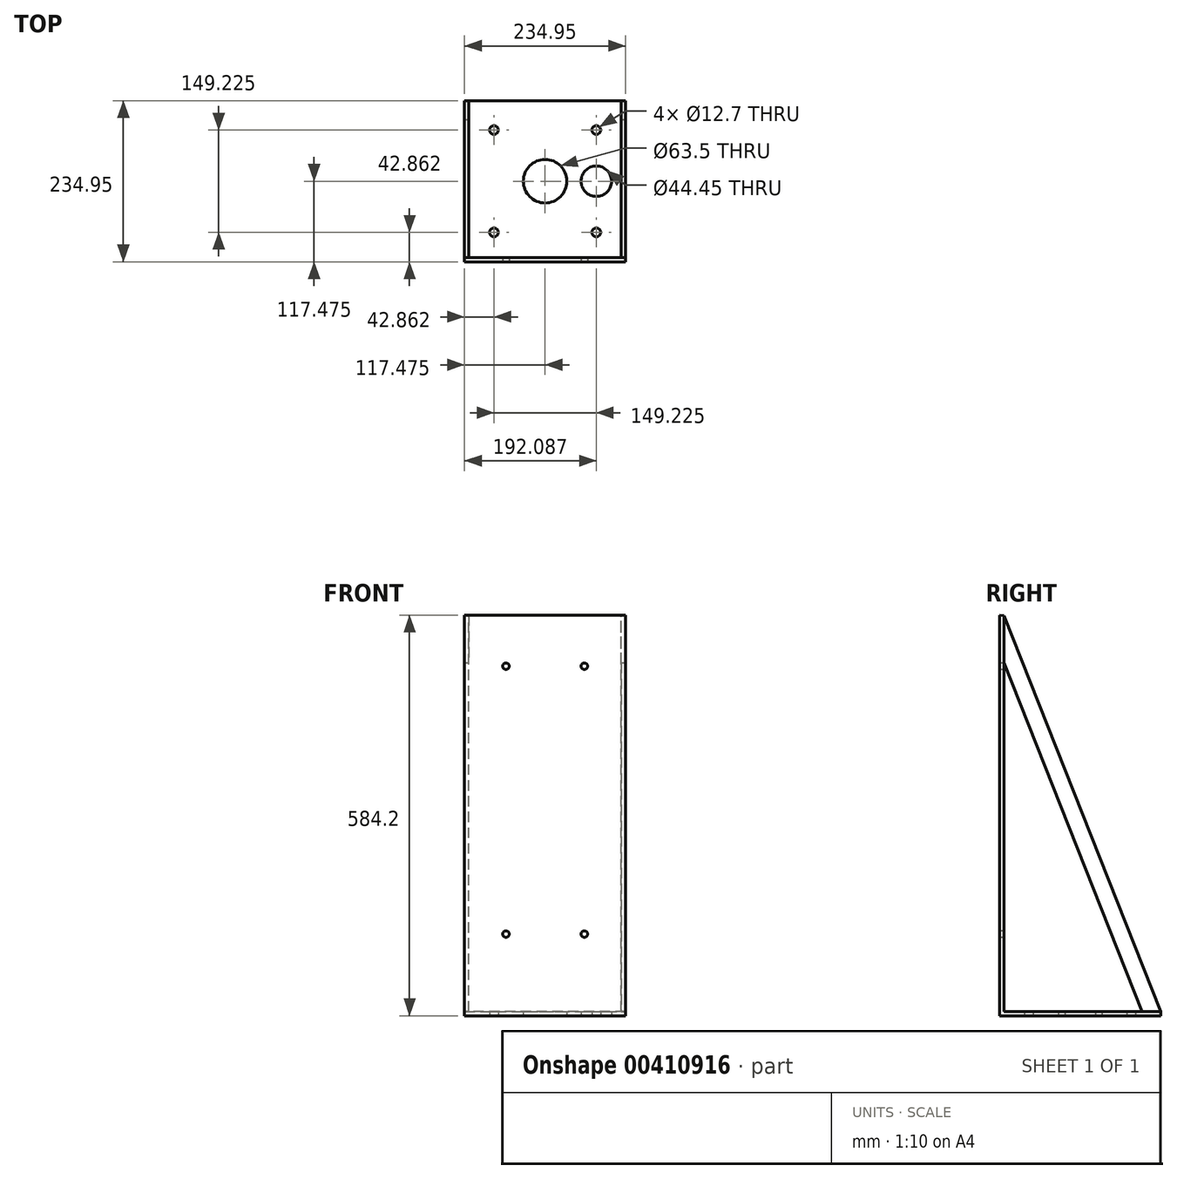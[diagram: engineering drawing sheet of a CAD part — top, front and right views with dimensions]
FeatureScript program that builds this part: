
annotation { "Feature Type Name" : "Feature", "Feature Type Description" : "" }
export const myFeature = defineFeature(function(context is Context, id is Id, definition is map)
    precondition{}
    {
        {
            var Q0;
            Q0=qCreatedBy(makeId("Top.planeOp"),FACE);
            var sketch = newSketch(context, id + "F0", { "sketchPlane" : qUnion([Q0])});
            skLineSegment(sketch, "E0", {"start": v(0, 0) * mm, "end": v(-234.95, 0) * mm});
            skLineSegment(sketch, "E1", {"start": v(-234.95, 0) * mm, "end": v(-234.95, 234.95) * mm});
            skLineSegment(sketch, "E2", {"start": v(-234.95, 234.95) * mm, "end": v(0, 234.95) * mm});
            skLineSegment(sketch, "E3", {"start": v(0, 234.95) * mm, "end": v(0, 0) * mm});
            skSolve(sketch);
        }
        {
            var Q0;
            Q0=qSketchRegion(id+"F0",true);
            extrude(context, id + "F1", {"entities" : qUnion([Q0]), "depth" : 584.2 * mm});
        }
        {
            var Q0;
            Q0=makeQuery(id+"F1.opExtrude","SWEPT_FACE",FACE,{"disambiguationData":[OSD([sQuery(id+"F0.wireOp",EDGE,"E3")])]});
            var sketch = newSketch(context, id + "F2", { "sketchPlane" : qUnion([Q0])});
            skLineSegment(sketch, "E4", {"start": v(234.95, 558.8) * mm, "end": v(0, 584.2) * mm});
            skLineSegment(sketch, "E5", {"start": v(234.95, 558.8) * mm, "end": v(234.95, 584.2) * mm});
            skLineSegment(sketch, "E6", {"start": v(234.95, 584.2) * mm, "end": v(0, 584.2) * mm});
            skSolve(sketch);
        }
        {
            var Q0;
            Q0=makeQuery(id+"F2.imprint","IMPRINT",FACE,{"disambiguationData":[TD([[makeQuery(id+"F2.imprint","IMPRINT",EDGE,{"derivedFrom":sQuery(id+"F2.wireOp",EDGE,"E4")}),-1.0]])]});
            extrude(context, id + "F3", {"entities" : qUnion([Q0]), "operationType" : NewBodyOperationType.REMOVE, "endBound" : BoundingType.THROUGH_ALL, "oppositeDirection" : true, "depth" : 25.4 * mm});
        }
        {
            var Q0;
            {var subQ0=sQuery(id+"F0.wireOp",EDGE,"E0");Q0=makeQuery(id+"FEAy7TYS6UcWf4X_1.boolean.opBoolean","MERGE",FACE,{"derivedFrom":[makeQuery(id+"F1.opExtrude","SWEPT_FACE",FACE,{"disambiguationData":[OSD([subQ0])]}),makeQuery(id+"FEAy7TYS6UcWf4X_1.opExtrude","SWEPT_FACE",FACE,{"disambiguationData":[OSD([subQ0])]})]});}
            var sketch = newSketch(context, id + "F4", { "sketchPlane" : qUnion([Q0])});
            skLineSegment(sketch, "E7", {"start": v(-117.48, 0) * mm, "end": v(-117.48, 509.59) * mm});
            skPoint(sketch, "E8.endSnap0", {"position": v(-117.47, 584.2) * mm});
            skLineSegment(sketch, "E9", {"start": v(-117.48, 509.59) * mm, "end": v(-60.33, 509.59) * mm});
            skLineSegment(sketch, "E10", {"start": v(-117.48, 509.59) * mm, "end": v(-174.63, 509.59) * mm});
            skCircle(sketch, "E11", {"center": v(-60.33, 509.59) * mm, "radius": 4.76 * mm});
            skCircle(sketch, "E12", {"center": v(-174.63, 509.59) * mm, "radius": 4.76 * mm});
            skLineSegment(sketch, "E13", {"start": v(-174.63, 509.59) * mm, "end": v(-174.62, 119.06) * mm});
            skLineSegment(sketch, "E14", {"start": v(-60.33, 509.59) * mm, "end": v(-60.33, 119.06) * mm});
            skCircle(sketch, "E15", {"center": v(-174.62, 119.06) * mm, "radius": 4.76 * mm});
            skCircle(sketch, "E16", {"center": v(-60.33, 119.06) * mm, "radius": 4.76 * mm});
            skSolve(sketch);
        }
        {
            var Q0;
            Q0=qSketchRegion(id+"F4",true);
            extrude(context, id + "F5", {"entities" : qUnion([Q0]), "operationType" : NewBodyOperationType.REMOVE, "oppositeDirection" : true, "depth" : 25.4 * mm});
        }
        {
            var Q0;
            Q0=qSketchRegion(id+"F4",true);
            extrude(context, id + "F6", {"entities" : qUnion([Q0]), "operationType" : NewBodyOperationType.REMOVE, "oppositeDirection" : true, "depth" : 25.4 * mm});
        }
        {
            var Q0;
            Q0=makeQuery(id+"F1.opExtrude","SWEPT_FACE",FACE,{"disambiguationData":[OSD([sQuery(id+"F0.wireOp",EDGE,"E3")])]});
            var sketch = newSketch(context, id + "F7", { "sketchPlane" : qUnion([Q0])});
            skLineSegment(sketch, "E17", {"start": v(0, 0) * mm, "end": v(6.35, 0) * mm});
            skLineSegment(sketch, "E18", {"start": v(6.35, 0) * mm, "end": v(6.35, 6.35) * mm});
            skLineSegment(sketch, "E19.bottom", {"start": v(6.35, 6.35) * mm, "end": v(445.92, 6.35) * mm});
            skLineSegment(sketch, "E19.top", {"start": v(6.35, 612) * mm, "end": v(445.92, 612) * mm});
            skLineSegment(sketch, "E19.left", {"start": v(6.35, 6.35) * mm, "end": v(6.35, 612) * mm});
            skLineSegment(sketch, "E19.right", {"start": v(445.92, 6.35) * mm, "end": v(445.92, 612) * mm});
            skSolve(sketch);
        }
        {
            var Q0;
            Q0 = qSketchRegion(id + "F7", true);
            extrude(context, id + "F8", {"entities" : qUnion([Q0]), "operationType" : NewBodyOperationType.REMOVE, "endBound" : BoundingType.THROUGH_ALL, "oppositeDirection" : true, "depth" : 25.4 * mm});
        }
        {
            var Q0;
            Q0=makeQuery(id+"F1.opExtrude","SWEPT_FACE",FACE,{"disambiguationData":[OSD([sQuery(id+"F0.wireOp",EDGE,"E3")])]});
            var sketch = newSketch(context, id + "F9", { "sketchPlane" : qUnion([Q0])});
            skLineSegment(sketch, "E20", {"start": v(6.35, 583.51) * mm, "end": v(6.35, 6.35) * mm});
            skLineSegment(sketch, "E21", {"start": v(6.35, 6.35) * mm, "end": v(234.95, 6.35) * mm});
            skLineSegment(sketch, "E22", {"start": v(234.95, 6.35) * mm, "end": v(6.35, 583.51) * mm});
            skSolve(sketch);
        }
        {
            var Q0;
            Q0 = qSketchRegion(id + "F9", true);
            extrude(context, id + "F10", {"entities" : qUnion([Q0]), "oppositeDirection" : true, "depth" : 6.35 * mm});
        }
        {
            var Q0;
            Q0=makeQuery(id+"F1.opExtrude","SWEPT_FACE",FACE,{"disambiguationData":[OSD([sQuery(id+"F0.wireOp",EDGE,"E1")])]});
            var sketch = newSketch(context, id + "F11", { "sketchPlane" : qUnion([Q0])});
            skLineSegment(sketch, "E23", {"start": v(-6.35, 583.51) * mm, "end": v(-6.35, 6.35) * mm});
            skLineSegment(sketch, "E24", {"start": v(-6.35, 6.35) * mm, "end": v(-234.95, 6.35) * mm});
            skLineSegment(sketch, "E25", {"start": v(-234.95, 6.35) * mm, "end": v(-6.35, 583.51) * mm});
            skSolve(sketch);
        }
        {
            var Q0;
            Q0 = qSketchRegion(id + "F11", true);
            extrude(context, id + "F12", {"entities" : qUnion([Q0]), "operationType" : NewBodyOperationType.ADD, "oppositeDirection" : true, "depth" : 6.35 * mm});
        }
        {
            var Q0;
            Q0=makeQuery(id+"F1.opExtrude","CAP_FACE",FACE,{"disambiguationData":[OSD([sQuery(id+"F0.wireOp",EDGE,"E0"),sQuery(id+"F0.wireOp",EDGE,"E1"),sQuery(id+"F0.wireOp",EDGE,"E2"),sQuery(id+"F0.wireOp",EDGE,"E3")])],"isStart":true});
            var sketch = newSketch(context, id + "F13", { "sketchPlane" : qUnion([Q0])});
            skCircle(sketch, "E26", {"center": v(-192.09, -42.86) * mm, "radius": 6.35 * mm});
            skCircle(sketch, "E27", {"center": v(-42.86, -42.86) * mm, "radius": 6.35 * mm});
            skCircle(sketch, "E28", {"center": v(-42.86, -192.09) * mm, "radius": 6.35 * mm});
            skCircle(sketch, "E29", {"center": v(-192.09, -192.09) * mm, "radius": 6.35 * mm});
            skCircle(sketch, "E30", {"center": v(-42.86, -117.48) * mm, "radius": 22.23 * mm});
            skCircle(sketch, "E31", {"center": v(-117.47, -117.48) * mm, "radius": 31.75 * mm});
            skSolve(sketch);
        }
        {
            var Q0;
            Q0 = qSketchRegion(id + "F13", true);
            extrude(context, id + "F14", {"entities" : qUnion([Q0]), "operationType" : NewBodyOperationType.REMOVE, "endBound" : BoundingType.THROUGH_ALL, "oppositeDirection" : true, "depth" : 25.4 * mm});
        }
        {
            var Q0;
            Q0 = qSketchRegion(id + "F13", true);
            extrude(context, id + "F15", {"entities" : qUnion([Q0]), "operationType" : NewBodyOperationType.REMOVE, "oppositeDirection" : true, "depth" : 25.4 * mm});
        }
        {
            var Q0;
            Q0=makeQuery(id+"F10.opExtrude","CAP_FACE",FACE,{"disambiguationData":[OSD([sQuery(id+"F9.wireOp",EDGE,"E20"),sQuery(id+"F9.wireOp",EDGE,"E21"),sQuery(id+"F9.wireOp",EDGE,"E22")])],"isStart":true});
            var sketch = newSketch(context, id + "F16", { "sketchPlane" : qUnion([Q0])});
            skLineSegment(sketch, "E32", {"start": v(97.03, 285.58) * mm, "end": v(6.35, 514.54) * mm});
            skLineSegment(sketch, "E33", {"start": v(97.03, 285.58) * mm, "end": v(207.63, 6.35) * mm});
            skSolve(sketch);
        }
        {
            var Q0;
            {var subQ0=sQuery(id+"F16.wireOp",EDGE,"E32");Q0=makeQuery(id+"F16.imprint","IMPRINT",FACE,{"disambiguationData":[TD([[makeQuery(id+"F16.imprint","IMPRINT",EDGE,{"derivedFrom":subQ0}),1.0]])]});}
            extrude(context, id + "F17", {"entities" : qUnion([Q0]), "operationType" : NewBodyOperationType.REMOVE, "endBound" : BoundingType.THROUGH_ALL, "oppositeDirection" : true, "depth" : 254 * mm});
        }
        {
            var Q0;
            Q0=makeQuery(id+"F12.boolean.opBoolean","MERGE",FACE,{"derivedFrom":[makeQuery(id+"F1.opExtrude","SWEPT_FACE",FACE,{"disambiguationData":[OSD([sQuery(id+"F0.wireOp",EDGE,"E1")])]}),makeQuery(id+"F12.opExtrude","CAP_FACE",FACE,{"disambiguationData":[OSD([sQuery(id+"F11.wireOp",EDGE,"E23"),sQuery(id+"F11.wireOp",EDGE,"E24"),sQuery(id+"F11.wireOp",EDGE,"E25")])],"isStart":true})]});
            var sketch = newSketch(context, id + "F18", { "sketchPlane" : qUnion([Q0])});
            skLineSegment(sketch, "E34", {"start": v(-97.03, 285.58) * mm, "end": v(-6.35, 514.54) * mm});
            skLineSegment(sketch, "E35", {"start": v(-6.35, 514.54) * mm, "end": v(-6.35, 6.35) * mm});
            skLineSegment(sketch, "E36", {"start": v(-97.03, 285.58) * mm, "end": v(-207.63, 6.35) * mm});
            skLineSegment(sketch, "E37", {"start": v(-207.63, 6.35) * mm, "end": v(-6.35, 6.35) * mm});
            skSolve(sketch);
        }
        {
            var Q0;
            Q0=makeQuery(id+"F18.imprint","IMPRINT",FACE,{"disambiguationData":[TD([[makeQuery(id+"F18.imprint","IMPRINT",EDGE,{"derivedFrom":sQuery(id+"F18.wireOp",EDGE,"E34")}),-1.0]])]});
            extrude(context, id + "F19", {"entities" : qUnion([Q0]), "operationType" : NewBodyOperationType.REMOVE, "endBound" : BoundingType.THROUGH_ALL, "oppositeDirection" : true, "depth" : 25.4 * mm});
        }
    });
